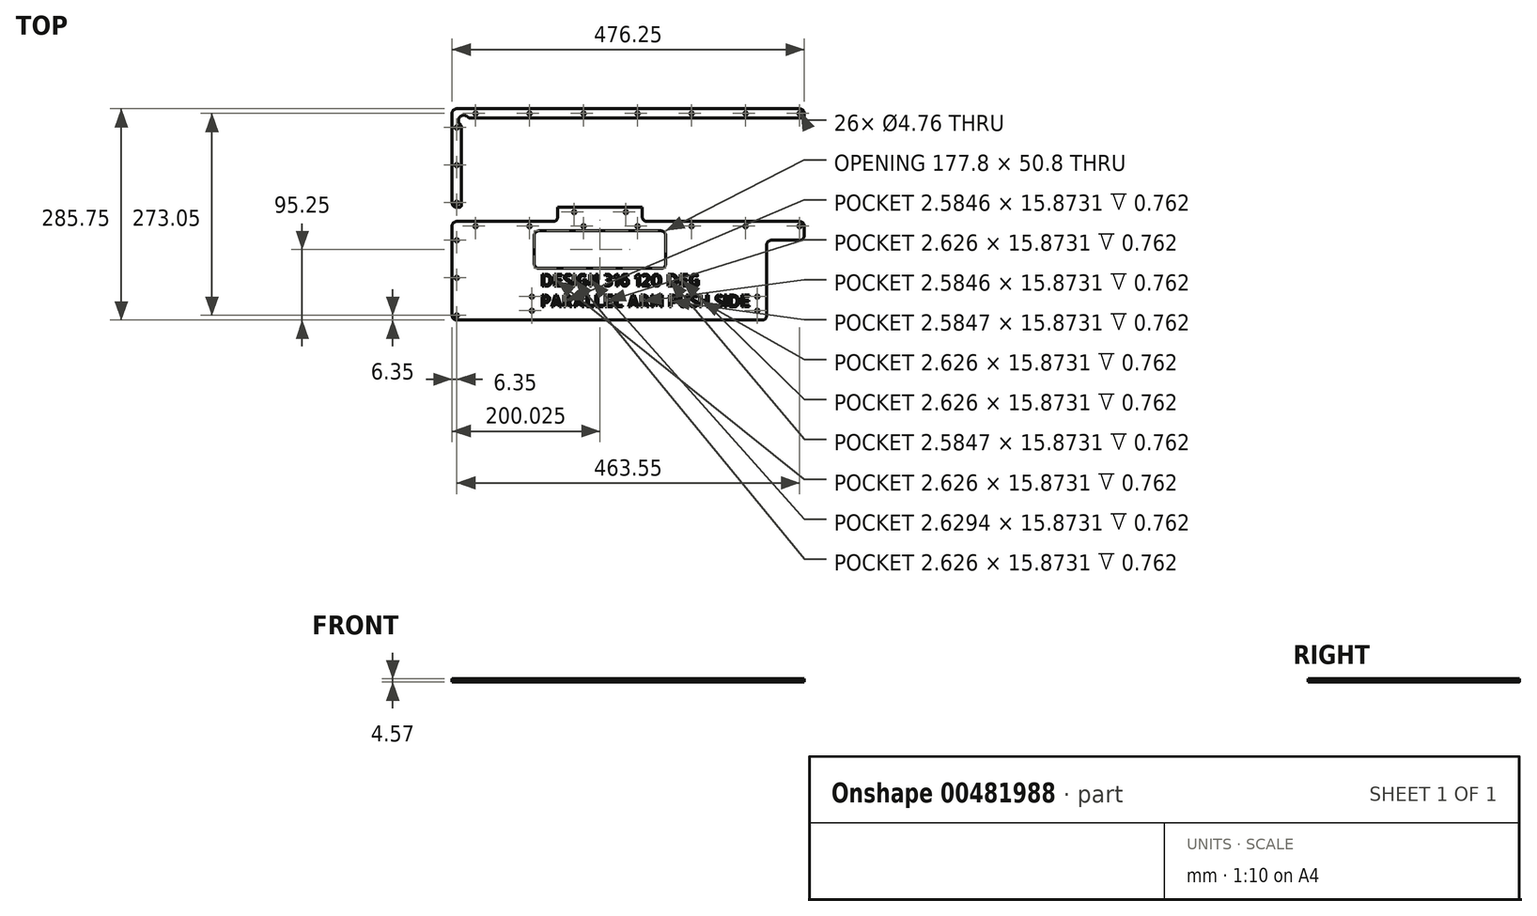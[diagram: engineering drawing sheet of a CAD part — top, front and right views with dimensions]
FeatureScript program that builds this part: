
annotation { "Feature Type Name" : "Feature", "Feature Type Description" : "" }
export const myFeature = defineFeature(function(context is Context, id is Id, definition is map)
    precondition{}
    {
        {
            var Q0;
            Q0=qCreatedBy(makeId("Top.planeOp"),FACE);
            var sketch = newSketch(context, id + "F0", { "sketchPlane" : qUnion([Q0])});
            skCircle(sketch, "E0", {"center": v(107.95, 12.7) * mm, "radius": 2.38 * mm});
            skLineSegment(sketch, "E1.bottom", {"start": v(107.95, 12.7) * mm, "end": v(412.75, 12.7) * mm, "construction": true});
            skLineSegment(sketch, "E1.top", {"start": v(107.95, 31.75) * mm, "end": v(412.75, 31.75) * mm, "construction": true});
            skLineSegment(sketch, "E1.left", {"start": v(107.95, 12.7) * mm, "end": v(107.95, 31.75) * mm, "construction": true});
            skLineSegment(sketch, "E1.right", {"start": v(412.75, 12.7) * mm, "end": v(412.75, 31.75) * mm, "construction": true});
            skCircle(sketch, "E2", {"center": v(107.95, 31.75) * mm, "radius": 2.38 * mm});
            skCircle(sketch, "E3", {"center": v(412.75, 31.75) * mm, "radius": 2.38 * mm});
            skCircle(sketch, "E4", {"center": v(412.75, 12.7) * mm, "radius": 2.38 * mm});
            skLineSegment(sketch, "E5", {"start": v(165.1, 146.05) * mm, "end": v(234.95, 146.05) * mm, "construction": true});
            skLineSegment(sketch, "E6", {"start": v(234.95, 146.05) * mm, "end": v(225.43, 157.16) * mm, "construction": true});
            skLineSegment(sketch, "E7", {"start": v(225.42, 157.16) * mm, "end": v(174.62, 157.16) * mm, "construction": true});
            skLineSegment(sketch, "E8", {"start": v(174.63, 157.16) * mm, "end": v(165.1, 146.05) * mm, "construction": true});
            skCircle(sketch, "E9", {"center": v(165.1, 146.05) * mm, "radius": 2.38 * mm});
            skCircle(sketch, "E10", {"center": v(174.62, 157.16) * mm, "radius": 2.38 * mm});
            skCircle(sketch, "E11", {"center": v(225.42, 157.16) * mm, "radius": 2.38 * mm});
            skCircle(sketch, "E12", {"center": v(234.95, 146.05) * mm, "radius": 2.38 * mm});
            skLineSegment(sketch, "E13.bottom", {"start": v(6.35, 0) * mm, "end": v(419.1, 0) * mm});
            skLineSegment(sketch, "E13.top", {"start": v(6.35, 133.35) * mm, "end": v(136.53, 133.35) * mm});
            skLineSegment(sketch, "E13.left", {"start": v(0, 6.35) * mm, "end": v(0, 127) * mm});
            skLineSegment(sketch, "E13.right", {"start": v(476.25, 114.3) * mm, "end": v(476.25, 127) * mm});
            skLineSegment(sketch, "E14.top", {"start": v(149.22, 171.45) * mm, "end": v(250.83, 171.45) * mm});
            skLineSegment(sketch, "E14.left", {"start": v(142.87, 139.7) * mm, "end": v(142.87, 165.1) * mm});
            skLineSegment(sketch, "E14.right", {"start": v(257.17, 139.7) * mm, "end": v(257.17, 165.1) * mm});
            skLineSegment(sketch, "E15.trimOffspring", {"start": v(263.52, 133.35) * mm, "end": v(469.9, 133.35) * mm});
            skLineSegment(sketch, "E16.0", {"start": v(6.35, 127) * mm, "end": v(467.52, 127) * mm, "construction": true});
            skLineSegment(sketch, "E17.0", {"start": v(12.7, 120.65) * mm, "end": v(476.25, 120.65) * mm, "construction": true});
            skLineSegment(sketch, "E17.1", {"start": v(12.7, 0) * mm, "end": v(12.7, 120.65) * mm, "construction": true});
            skLineSegment(sketch, "E18", {"start": v(469.9, 107.95) * mm, "end": v(431.8, 107.95) * mm});
            skLineSegment(sketch, "E19", {"start": v(425.45, 101.6) * mm, "end": v(425.45, 6.35) * mm});
            skLineSegment(sketch, "E20", {"start": v(200.02, 146.05) * mm, "end": v(200.02, 171.45) * mm, "construction": true});
            skPoint(sketch, "E21.visualSharp", {"position": v(0, 133.35) * mm});
            skArc(sketch, "E21.filletArc", {"start": v(6.35, 133.35) * mm, "mid": v(1.86, 131.5) * mm, "end": v(0, 127) * mm});
            skPoint(sketch, "E22.visualSharp", {"position": v(0, 0) * mm});
            skArc(sketch, "E22.filletArc", {"start": v(0, 6.35) * mm, "mid": v(1.86, 1.86) * mm, "end": v(6.35, 0) * mm});
            skPoint(sketch, "E23.visualSharp", {"position": v(425.45, 0) * mm});
            skArc(sketch, "E23.filletArc", {"start": v(419.1, 0) * mm, "mid": v(423.6, 1.86) * mm, "end": v(425.45, 6.35) * mm});
            skPoint(sketch, "E24.visualSharp", {"position": v(425.45, 107.95) * mm});
            skArc(sketch, "E24.filletArc", {"start": v(431.8, 107.95) * mm, "mid": v(427.3, 106.1) * mm, "end": v(425.45, 101.6) * mm});
            skPoint(sketch, "E25.visualSharp", {"position": v(476.25, 107.95) * mm});
            skArc(sketch, "E25.filletArc", {"start": v(469.9, 107.95) * mm, "mid": v(474.4, 109.8) * mm, "end": v(476.25, 114.3) * mm});
            skPoint(sketch, "E26.visualSharp", {"position": v(476.25, 133.35) * mm});
            skArc(sketch, "E26.filletArc", {"start": v(476.25, 127) * mm, "mid": v(474.4, 131.5) * mm, "end": v(469.9, 133.35) * mm});
            skPoint(sketch, "E27.visualSharp", {"position": v(257.17, 133.35) * mm});
            skArc(sketch, "E27.filletArc", {"start": v(257.17, 139.7) * mm, "mid": v(259.03, 135.2) * mm, "end": v(263.52, 133.35) * mm});
            skPoint(sketch, "E28.visualSharp", {"position": v(257.18, 171.45) * mm});
            skArc(sketch, "E28.filletArc", {"start": v(257.18, 165.1) * mm, "mid": v(255.32, 169.6) * mm, "end": v(250.83, 171.45) * mm});
            skPoint(sketch, "E29.visualSharp", {"position": v(142.87, 171.45) * mm});
            skArc(sketch, "E29.filletArc", {"start": v(149.22, 171.45) * mm, "mid": v(144.73, 169.6) * mm, "end": v(142.87, 165.1) * mm});
            skPoint(sketch, "E30.visualSharp", {"position": v(142.87, 133.35) * mm});
            skArc(sketch, "E30.filletArc", {"start": v(136.53, 133.35) * mm, "mid": v(141.02, 135.2) * mm, "end": v(142.87, 139.7) * mm});
            skCircle(sketch, "E31", {"center": v(6.35, 6.35) * mm, "radius": 2.38 * mm});
            skCircle(sketch, "E32", {"center": v(6.35, 57.15) * mm, "radius": 2.38 * mm});
            skCircle(sketch, "E33", {"center": v(6.35, 107.95) * mm, "radius": 2.38 * mm});
            skCircle(sketch, "E34", {"center": v(469.9, 127) * mm, "radius": 2.38 * mm});
            skLineSegment(sketch, "E35", {"start": v(6.35, 107.95) * mm, "end": v(6.35, 57.15) * mm, "construction": true});
            skLineSegment(sketch, "E36", {"start": v(6.35, 6.35) * mm, "end": v(6.35, 57.15) * mm, "construction": true});
            skCircle(sketch, "E37.1.0.0", {"center": v(396.88, 127) * mm, "radius": 2.38 * mm});
            skCircle(sketch, "E37.2.0.0", {"center": v(323.85, 127) * mm, "radius": 2.38 * mm});
            skCircle(sketch, "E37.3.0.0", {"center": v(250.83, 127) * mm, "radius": 2.38 * mm});
            skCircle(sketch, "E37.4.0.0", {"center": v(177.8, 127) * mm, "radius": 2.38 * mm});
            skCircle(sketch, "E37.5.0.0", {"center": v(104.78, 127) * mm, "radius": 2.38 * mm});
            skCircle(sketch, "E37.6.0.0", {"center": v(31.75, 127) * mm, "radius": 2.38 * mm});
            skLineSegment(sketch, "E37.direction1", {"start": v(469.9, 127) * mm, "end": v(396.88, 127) * mm, "construction": true});
            skLineSegment(sketch, "E38.bottom", {"start": v(117.47, 120.65) * mm, "end": v(282.58, 120.65) * mm});
            skLineSegment(sketch, "E38.top", {"start": v(117.47, 69.85) * mm, "end": v(282.58, 69.85) * mm});
            skLineSegment(sketch, "E38.left", {"start": v(111.12, 114.3) * mm, "end": v(111.12, 76.2) * mm});
            skLineSegment(sketch, "E38.right", {"start": v(288.93, 114.3) * mm, "end": v(288.93, 76.2) * mm});
            skLineSegment(sketch, "E39", {"start": v(200.02, 69.85) * mm, "end": v(200.02, 146.05) * mm, "construction": true});
            skPoint(sketch, "E40.visualSharp", {"position": v(111.12, 120.65) * mm});
            skArc(sketch, "E40.filletArc", {"start": v(117.47, 120.65) * mm, "mid": v(112.98, 118.8) * mm, "end": v(111.12, 114.3) * mm});
            skPoint(sketch, "E41.visualSharp", {"position": v(111.12, 69.85) * mm});
            skArc(sketch, "E41.filletArc", {"start": v(111.12, 76.2) * mm, "mid": v(112.98, 71.7) * mm, "end": v(117.47, 69.85) * mm});
            skPoint(sketch, "E42.visualSharp", {"position": v(288.93, 69.85) * mm});
            skArc(sketch, "E42.filletArc", {"start": v(282.58, 69.85) * mm, "mid": v(287.07, 71.7) * mm, "end": v(288.93, 76.2) * mm});
            skPoint(sketch, "E43.visualSharp", {"position": v(288.93, 120.65) * mm});
            skArc(sketch, "E43.filletArc", {"start": v(288.93, 114.3) * mm, "mid": v(287.07, 118.8) * mm, "end": v(282.58, 120.65) * mm});
            skSolve(sketch);
        }
        {
            var Q0;
            Q0 = qSketchRegion(id + "F0", true);
            extrude(context, id + "F1", {"entities" : qUnion([Q0]), "depth" : 4.57 * mm});
        }
        {
            var Q0;
            Q0=makeQuery(id+"F1.opExtrude","CAP_FACE",FACE,{"disambiguationData":[OSD([sQuery(id+"F0.wireOp",EDGE,"E0"),sQuery(id+"F0.wireOp",EDGE,"E2"),sQuery(id+"F0.wireOp",EDGE,"E3"),sQuery(id+"F0.wireOp",EDGE,"E4"),sQuery(id+"F0.wireOp",EDGE,"E9"),sQuery(id+"F0.wireOp",EDGE,"E10"),sQuery(id+"F0.wireOp",EDGE,"E11"),sQuery(id+"F0.wireOp",EDGE,"E12"),sQuery(id+"F0.wireOp",EDGE,"E13.bottom"),sQuery(id+"F0.wireOp",EDGE,"E13.top"),sQuery(id+"F0.wireOp",EDGE,"E13.left"),sQuery(id+"F0.wireOp",EDGE,"E13.right"),sQuery(id+"F0.wireOp",EDGE,"E14.top"),sQuery(id+"F0.wireOp",EDGE,"E14.left"),sQuery(id+"F0.wireOp",EDGE,"E14.right"),sQuery(id+"F0.wireOp",EDGE,"E15.trimOffspring"),sQuery(id+"F0.wireOp",EDGE,"E18"),sQuery(id+"F0.wireOp",EDGE,"E19"),sQuery(id+"F0.wireOp",EDGE,"E21.filletArc"),sQuery(id+"F0.wireOp",EDGE,"E22.filletArc"),sQuery(id+"F0.wireOp",EDGE,"E23.filletArc"),sQuery(id+"F0.wireOp",EDGE,"E24.filletArc"),sQuery(id+"F0.wireOp",EDGE,"E25.filletArc"),sQuery(id+"F0.wireOp",EDGE,"E26.filletArc"),sQuery(id+"F0.wireOp",EDGE,"E27.filletArc"),sQuery(id+"F0.wireOp",EDGE,"E28.filletArc"),sQuery(id+"F0.wireOp",EDGE,"E29.filletArc"),sQuery(id+"F0.wireOp",EDGE,"E30.filletArc"),sQuery(id+"F0.wireOp",EDGE,"E31"),sQuery(id+"F0.wireOp",EDGE,"E32"),sQuery(id+"F0.wireOp",EDGE,"E33"),sQuery(id+"F0.wireOp",EDGE,"E34"),sQuery(id+"F0.wireOp",EDGE,"E37.1.0.0"),sQuery(id+"F0.wireOp",EDGE,"E37.2.0.0"),sQuery(id+"F0.wireOp",EDGE,"E37.3.0.0"),sQuery(id+"F0.wireOp",EDGE,"E37.4.0.0"),sQuery(id+"F0.wireOp",EDGE,"E37.5.0.0"),sQuery(id+"F0.wireOp",EDGE,"E37.6.0.0"),sQuery(id+"F0.wireOp",EDGE,"E38.bottom"),sQuery(id+"F0.wireOp",EDGE,"E38.top"),sQuery(id+"F0.wireOp",EDGE,"E38.left"),sQuery(id+"F0.wireOp",EDGE,"E38.right"),sQuery(id+"F0.wireOp",EDGE,"E40.filletArc"),sQuery(id+"F0.wireOp",EDGE,"E41.filletArc"),sQuery(id+"F0.wireOp",EDGE,"E42.filletArc"),sQuery(id+"F0.wireOp",EDGE,"E43.filletArc")])],"isStart":false});
            var sketch = newSketch(context, id + "F2", { "sketchPlane" : qUnion([Q0])});
            skText(sketch, "E44", { "text": "DESIGN 316 120 DEG\nPARALLEL ARM PUSH SIDE\n", "fontName": "AllertaStencil-Regular.ttf"});
            const initialGuessF2  = {"E44": [0.1199, 0.04604, 1, 0, 0.01588]};
            skSetInitialGuess(sketch, initialGuessF2);
            skSolve(sketch);
        }
        {
            var Q0;
            Q0 = qSketchRegion(id + "F2", true);
            var Q1;
            Q1 = qConstructionFilter(qBodyType(qCreatedBy(id + "F2" ,EDGE), BodyType.WIRE), ConstructionObject.NO);
            extrude(context, id + "F3", {"entities" : qUnion([Q0]), "operationType" : NewBodyOperationType.REMOVE, "surfaceEntities" : qUnion([Q1]), "oppositeDirection" : true, "depth" : 0.76 * mm});
        }
        {
            var Q0;
            Q0=makeQuery(id+"F1.opExtrude","SWEPT_BODY",BODY,{"disambiguationData":[OSD([sQuery(id+"F0.wireOp",EDGE,"E0"),sQuery(id+"F0.wireOp",EDGE,"E2"),sQuery(id+"F0.wireOp",EDGE,"E3"),sQuery(id+"F0.wireOp",EDGE,"E4"),sQuery(id+"F0.wireOp",EDGE,"E9"),sQuery(id+"F0.wireOp",EDGE,"E10"),sQuery(id+"F0.wireOp",EDGE,"E11"),sQuery(id+"F0.wireOp",EDGE,"E12"),sQuery(id+"F0.wireOp",EDGE,"E13.bottom"),sQuery(id+"F0.wireOp",EDGE,"E13.top"),sQuery(id+"F0.wireOp",EDGE,"E13.left"),sQuery(id+"F0.wireOp",EDGE,"E13.right"),sQuery(id+"F0.wireOp",EDGE,"E14.top"),sQuery(id+"F0.wireOp",EDGE,"E14.left"),sQuery(id+"F0.wireOp",EDGE,"E14.right"),sQuery(id+"F0.wireOp",EDGE,"E15.trimOffspring"),sQuery(id+"F0.wireOp",EDGE,"E18"),sQuery(id+"F0.wireOp",EDGE,"E19"),sQuery(id+"F0.wireOp",EDGE,"E21.filletArc"),sQuery(id+"F0.wireOp",EDGE,"E22.filletArc"),sQuery(id+"F0.wireOp",EDGE,"E23.filletArc"),sQuery(id+"F0.wireOp",EDGE,"E24.filletArc"),sQuery(id+"F0.wireOp",EDGE,"E25.filletArc"),sQuery(id+"F0.wireOp",EDGE,"E26.filletArc"),sQuery(id+"F0.wireOp",EDGE,"E27.filletArc"),sQuery(id+"F0.wireOp",EDGE,"E28.filletArc"),sQuery(id+"F0.wireOp",EDGE,"E29.filletArc"),sQuery(id+"F0.wireOp",EDGE,"E30.filletArc"),sQuery(id+"F0.wireOp",EDGE,"E31"),sQuery(id+"F0.wireOp",EDGE,"E32"),sQuery(id+"F0.wireOp",EDGE,"E33"),sQuery(id+"F0.wireOp",EDGE,"E34"),sQuery(id+"F0.wireOp",EDGE,"E37.1.0.0"),sQuery(id+"F0.wireOp",EDGE,"E37.2.0.0"),sQuery(id+"F0.wireOp",EDGE,"E37.3.0.0"),sQuery(id+"F0.wireOp",EDGE,"E37.4.0.0"),sQuery(id+"F0.wireOp",EDGE,"E37.5.0.0"),sQuery(id+"F0.wireOp",EDGE,"E37.6.0.0"),sQuery(id+"F0.wireOp",EDGE,"E38.bottom"),sQuery(id+"F0.wireOp",EDGE,"E38.top"),sQuery(id+"F0.wireOp",EDGE,"E38.left"),sQuery(id+"F0.wireOp",EDGE,"E38.right"),sQuery(id+"F0.wireOp",EDGE,"E40.filletArc"),sQuery(id+"F0.wireOp",EDGE,"E41.filletArc"),sQuery(id+"F0.wireOp",EDGE,"E42.filletArc"),sQuery(id+"F0.wireOp",EDGE,"E43.filletArc")])]});
            transform(context, id + "F4", {"entities" : qUnion([Q0]), "transformType" : TransformType.TRANSLATION_3D, "dx" : 0 * mm, "dy" : 152.4 * mm, "dz" : 0 * mm, "makeCopy" : true});
        }
        {
            var Q0;
            {var subQ0=sQuery(id+"F0.wireOp",EDGE,"E42.filletArc");var subQ1=sQuery(id+"F0.wireOp",EDGE,"E41.filletArc");var subQ2=sQuery(id+"F0.wireOp",EDGE,"E38.right");var subQ3=sQuery(id+"F0.wireOp",EDGE,"E38.left");var subQ4=sQuery(id+"F0.wireOp",EDGE,"E38.top");var subQ5=sQuery(id+"F0.wireOp",EDGE,"E38.bottom");var subQ6=sQuery(id+"F0.wireOp",EDGE,"E37.6.0.0");var subQ7=sQuery(id+"F0.wireOp",EDGE,"E37.5.0.0");var subQ8=sQuery(id+"F0.wireOp",EDGE,"E37.4.0.0");var subQ9=sQuery(id+"F0.wireOp",EDGE,"E40.filletArc");var subQ10=sQuery(id+"F0.wireOp",EDGE,"E30.filletArc");var subQ11=sQuery(id+"F0.wireOp",EDGE,"E29.filletArc");var subQ12=sQuery(id+"F0.wireOp",EDGE,"E37.3.0.0");var subQ13=sQuery(id+"F0.wireOp",EDGE,"E27.filletArc");var subQ14=sQuery(id+"F0.wireOp",EDGE,"E37.2.0.0");var subQ15=sQuery(id+"F0.wireOp",EDGE,"E26.filletArc");var subQ16=sQuery(id+"F0.wireOp",EDGE,"E37.1.0.0");var subQ17=sQuery(id+"F0.wireOp",EDGE,"E25.filletArc");var subQ18=sQuery(id+"F0.wireOp",EDGE,"E34");var subQ19=sQuery(id+"F0.wireOp",EDGE,"E13.bottom");var subQ20=sQuery(id+"F0.wireOp",EDGE,"E12");var subQ21=sQuery(id+"F0.wireOp",EDGE,"E11");var subQ22=sQuery(id+"F0.wireOp",EDGE,"E10");var subQ23=sQuery(id+"F0.wireOp",EDGE,"E9");var subQ24=sQuery(id+"F0.wireOp",EDGE,"E13.top");var subQ25=sQuery(id+"F0.wireOp",EDGE,"E43.filletArc");var subQ26=sQuery(id+"F0.wireOp",EDGE,"E0");var subQ27=sQuery(id+"F0.wireOp",EDGE,"E24.filletArc");var subQ28=sQuery(id+"F0.wireOp",EDGE,"E33");var subQ29=sQuery(id+"F0.wireOp",EDGE,"E4");var subQ30=sQuery(id+"F0.wireOp",EDGE,"E2");var subQ31=sQuery(id+"F0.wireOp",EDGE,"E3");var subQ32=sQuery(id+"F0.wireOp",EDGE,"E13.left");var subQ33=sQuery(id+"F0.wireOp",EDGE,"E13.right");var subQ34=sQuery(id+"F0.wireOp",EDGE,"E14.top");var subQ35=sQuery(id+"F0.wireOp",EDGE,"E14.left");var subQ36=sQuery(id+"F0.wireOp",EDGE,"E14.right");var subQ37=sQuery(id+"F0.wireOp",EDGE,"E15.trimOffspring");var subQ38=sQuery(id+"F0.wireOp",EDGE,"E18");var subQ39=sQuery(id+"F0.wireOp",EDGE,"E28.filletArc");var subQ40=sQuery(id+"F0.wireOp",EDGE,"E19");var subQ41=sQuery(id+"F0.wireOp",EDGE,"E21.filletArc");var subQ42=sQuery(id+"F0.wireOp",EDGE,"E22.filletArc");var subQ43=sQuery(id+"F0.wireOp",EDGE,"E31");var subQ44=sQuery(id+"F0.wireOp",EDGE,"E23.filletArc");var subQ45=sQuery(id+"F0.wireOp",EDGE,"E32");Q0=makeQuery(id+"F4.opPattern","COPY",FACE,{"derivedFrom":makeQuery(id+"F3.boolean.opBoolean","SPLIT",FACE,{"disambiguationData":[TD([makeQuery(id+"F1.opExtrude","SWEPT_FACE",FACE,{"disambiguationData":[OSD([subQ26])]})])],"derivedFrom":makeQuery(id+"F1.opExtrude","CAP_FACE",FACE,{"disambiguationData":[OSD([subQ26,subQ30,subQ31,subQ29,subQ23,subQ22,subQ21,subQ20,subQ19,subQ24,subQ32,subQ33,subQ34,subQ35,subQ36,subQ37,subQ38,subQ40,subQ41,subQ42,subQ44,subQ27,subQ17,subQ15,subQ13,subQ39,subQ11,subQ10,subQ43,subQ45,subQ28,subQ18,subQ16,subQ14,subQ12,subQ8,subQ7,subQ6,subQ5,subQ4,subQ3,subQ2,subQ9,subQ1,subQ0,subQ25])],"isStart":false})}),"instanceName":"1"});}
            var sketch = newSketch(context, id + "F5", { "sketchPlane" : qUnion([Q0])});
            skLineSegment(sketch, "E45.bottom", {"start": v(25.4, 273.05) * mm, "end": v(473.08, 273.05) * mm});
            skLineSegment(sketch, "E45.top", {"start": v(9.53, 152.4) * mm, "end": v(476.25, 152.4) * mm});
            skLineSegment(sketch, "E45.left", {"start": v(12.7, 260.35) * mm, "end": v(12.7, 155.58) * mm});
            skLineSegment(sketch, "E45.right", {"start": v(476.25, 276.22) * mm, "end": v(476.25, 152.4) * mm});
            skLineSegment(sketch, "E46.bottom", {"start": v(124.48, 345.42) * mm, "end": v(276.92, 345.42) * mm});
            skLineSegment(sketch, "E46.top", {"start": v(124.48, 285.75) * mm, "end": v(276.92, 285.75) * mm});
            skLineSegment(sketch, "E46.left", {"start": v(124.48, 345.42) * mm, "end": v(124.48, 285.75) * mm});
            skLineSegment(sketch, "E46.right", {"start": v(276.92, 345.42) * mm, "end": v(276.92, 285.75) * mm});
            skArc(sketch, "E47", {"start": v(20.9, 274.9) * mm, "mid": v(10.84, 274.9) * mm, "end": v(10.84, 264.84) * mm});
            skPoint(sketch, "E48.visualSharp", {"position": v(22.25, 273.05) * mm});
            skArc(sketch, "E48.filletArc", {"start": v(20.9, 274.9) * mm, "mid": v(22.97, 273.53) * mm, "end": v(25.4, 273.05) * mm});
            skPoint(sketch, "E49.visualSharp", {"position": v(12.7, 263.5) * mm});
            skArc(sketch, "E49.filletArc", {"start": v(12.7, 260.35) * mm, "mid": v(12.22, 262.78) * mm, "end": v(10.84, 264.84) * mm});
            skPoint(sketch, "E50.newPointA", {"position": v(476.25, 266.7) * mm});
            skArc(sketch, "E50.filletArc", {"start": v(473.08, 273.05) * mm, "mid": v(475.32, 273.98) * mm, "end": v(476.25, 276.22) * mm});
            skPoint(sketch, "E51.newPointB", {"position": v(419.1, 152.4) * mm});
            skArc(sketch, "E51.filletArc", {"start": v(9.53, 152.4) * mm, "mid": v(11.77, 153.33) * mm, "end": v(12.7, 155.58) * mm});
            skSolve(sketch);
        }
        {
            var Q0;
            Q0 = qSketchRegion(id + "F5", true);
            extrude(context, id + "F6", {"entities" : qUnion([Q0]), "operationType" : NewBodyOperationType.REMOVE, "endBound" : BoundingType.THROUGH_ALL, "oppositeDirection" : true, "depth" : 25.4 * mm});
        }
    });
